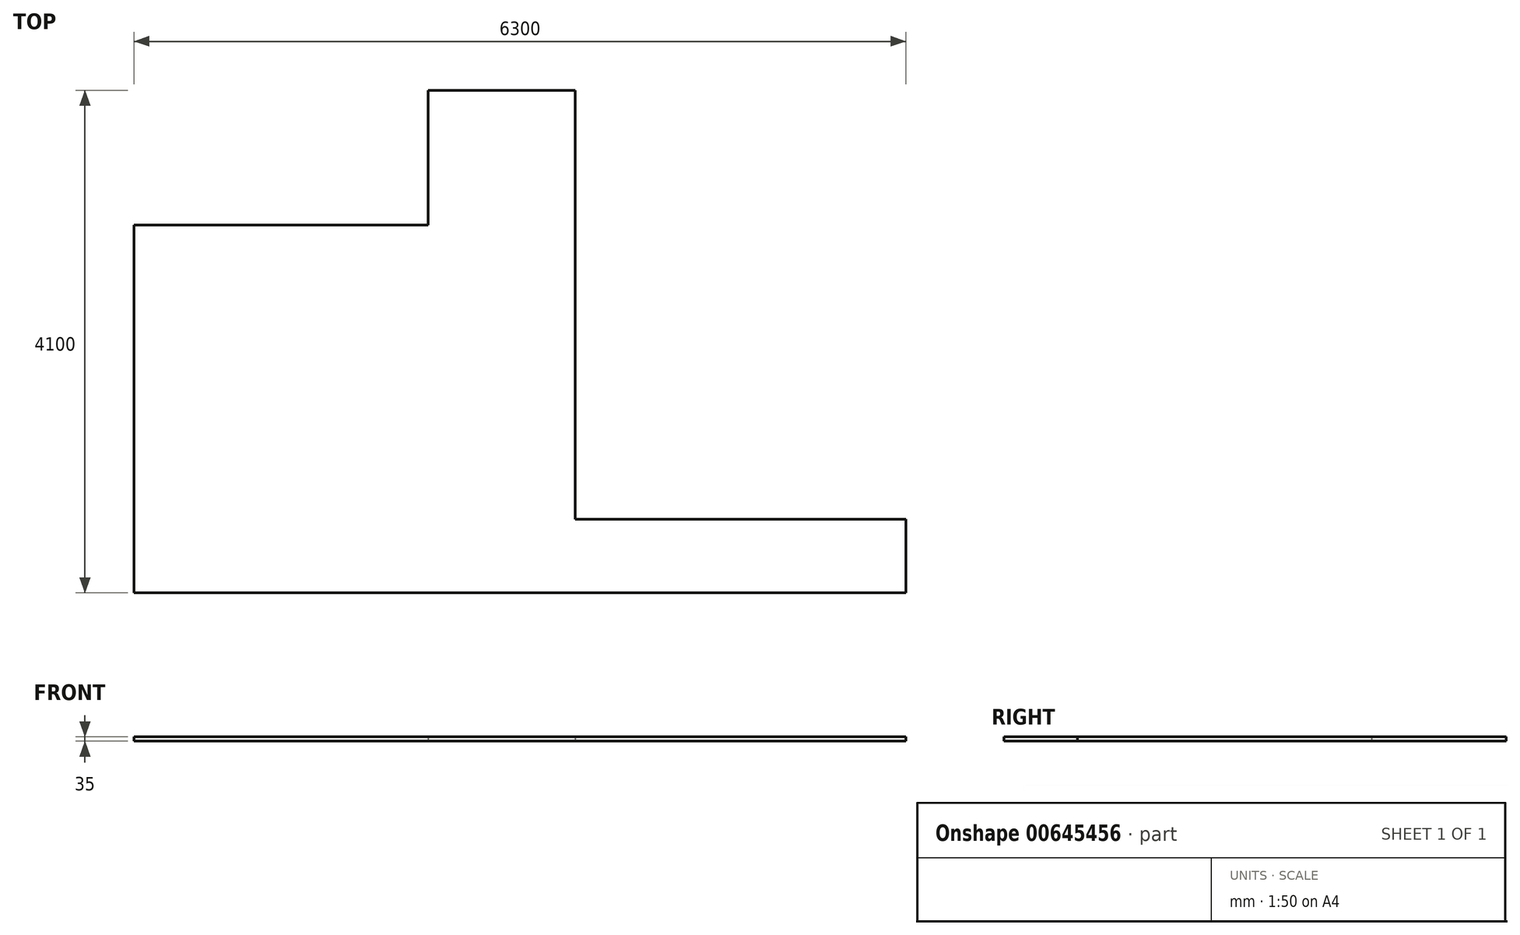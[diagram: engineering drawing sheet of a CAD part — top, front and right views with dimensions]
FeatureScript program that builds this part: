
annotation { "Feature Type Name" : "Feature", "Feature Type Description" : "" }
export const myFeature = defineFeature(function(context is Context, id is Id, definition is map)
    precondition{}
    {
        {
            var Q0;
            Q0=qCreatedBy(makeId("Top.planeOp"),FACE);
            var sketch = newSketch(context, id + "F0", { "sketchPlane" : qUnion([Q0])});
            skLineSegment(sketch, "E0", {"start": v(0, 0) * mm, "end": v(-6300, 0) * mm});
            skLineSegment(sketch, "E1", {"start": v(-6300, 0) * mm, "end": v(-6300, 3000) * mm});
            skLineSegment(sketch, "E2", {"start": v(-6300, 3000) * mm, "end": v(-3900, 3000) * mm});
            skLineSegment(sketch, "E3", {"start": v(-3900, 3000) * mm, "end": v(-3900, 4100) * mm});
            skLineSegment(sketch, "E4", {"start": v(-3900, 4100) * mm, "end": v(-2700, 4100) * mm});
            skLineSegment(sketch, "E5", {"start": v(-2700, 4100) * mm, "end": v(-2700, 600) * mm});
            skLineSegment(sketch, "E6", {"start": v(-2700, 600) * mm, "end": v(0, 600) * mm});
            skLineSegment(sketch, "E7", {"start": v(0, 600) * mm, "end": v(0, 0) * mm});
            skSolve(sketch);
        }
        {
            var Q0;
            Q0 = qSketchRegion(id + "F0", true);
            extrude(context, id + "F1", {"entities" : qUnion([Q0]), "depth" : 35 * mm, "offsetDistance" : 25 * mm});
        }
    });
